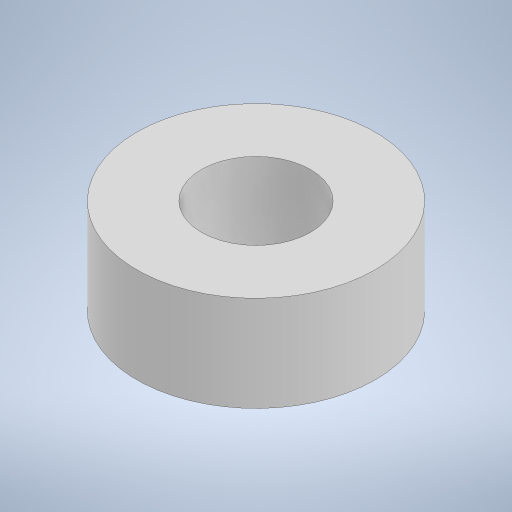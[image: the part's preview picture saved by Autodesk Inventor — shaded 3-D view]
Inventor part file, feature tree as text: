
AUTODESK INVENTOR PART (.ipt)
format: ipt  version: 2023 (Build 270158000, 158)  size: 201,728 bytes
history: native  units: mm
features: other x1, extrude x1, sketch x1
ambient origin geometry x8: Origin, YZ Plane, XZ Plane, XY Plane, X Axis, Y Axis, Z Axis, Center Point
bodies: Body1 (feature_tree)
feature tree (3):
  other  "Твердое тело1"
  extrude  "Выдавливание1"  Depth=16.0mm
  sketch  "Эскиз1"
